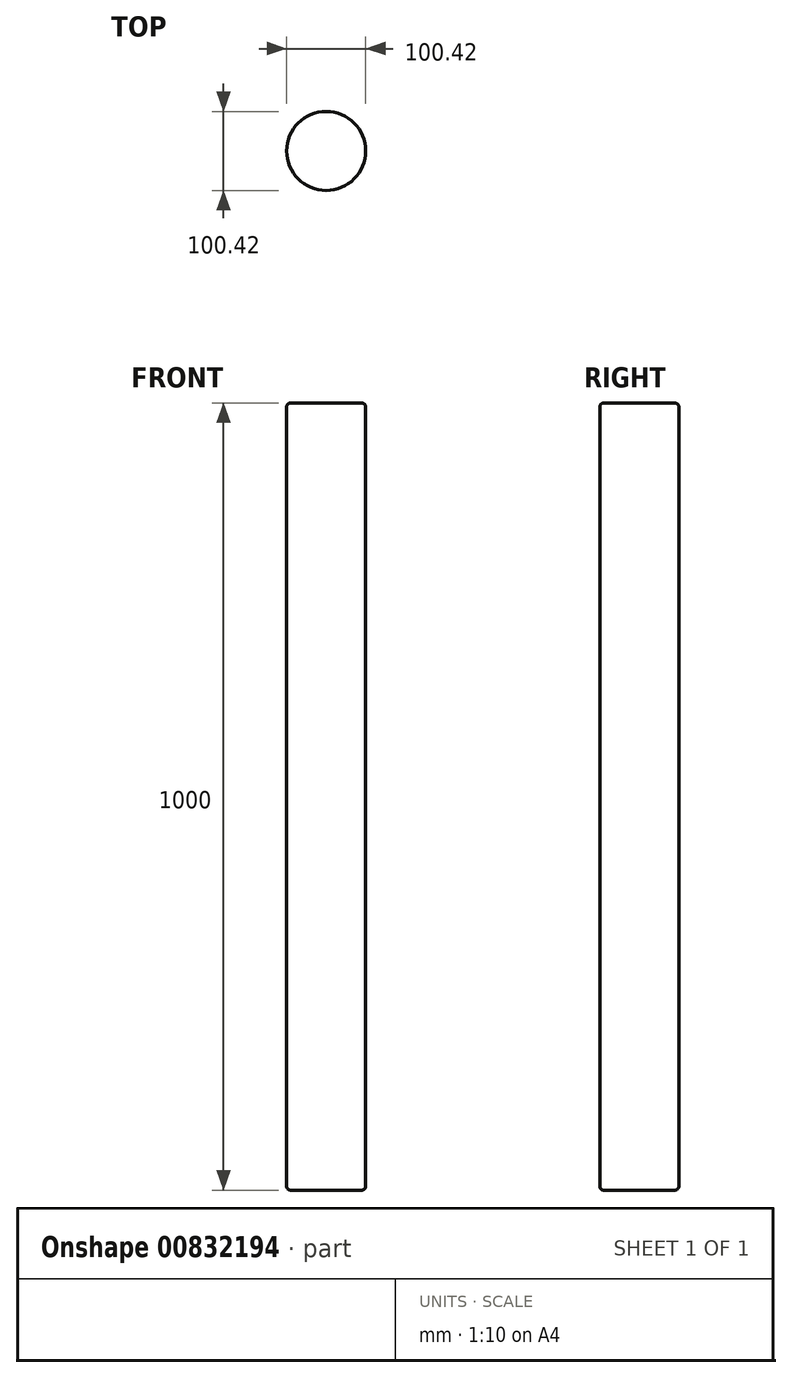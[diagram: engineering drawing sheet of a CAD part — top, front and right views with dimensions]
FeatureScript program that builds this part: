
annotation { "Feature Type Name" : "Feature", "Feature Type Description" : "" }
export const myFeature = defineFeature(function(context is Context, id is Id, definition is map)
    precondition{}
    {
        {
            var Q0;
            Q0=qCreatedBy(makeId("Top.planeOp"),FACE);
            var sketch = newSketch(context, id + "F0", { "sketchPlane" : qUnion([Q0])});
            skCircle(sketch, "E0", {"center": v(0, 0) * mm, "radius": 50.21 * mm});
            skSolve(sketch);
        }
        {
            var Q0;
            Q0 = qSketchRegion(id + "F0", true);
            extrude(context, id + "F1", {"entities" : qUnion([Q0]), "endBound" : BoundingType.SYMMETRIC, "oppositeDirection" : true, "depth" : 1000 * mm, "offsetDistance" : 25.4 * mm});
        }
        {
            var Q0;
            Q0=makeQuery(id+"F1.opExtrude","CAP_EDGE",EDGE,{"disambiguationData":[OSD([sQuery(id+"F0.wireOp",EDGE,"E0")])],"isStart":true});
            fillet(context, id + "F2", {"entities" : qUnion([Q0]), "radius" : 5.08 * mm, "tangentPropagation" : true, "allowEdgeOverflow" : false});
        }
        {
            var Q0;
            Q0=makeQuery(id+"F1.opExtrude","CAP_EDGE",EDGE,{"disambiguationData":[OSD([sQuery(id+"F0.wireOp",EDGE,"E0")])],"isStart":false});
            fillet(context, id + "F3", {"entities" : qUnion([Q0]), "radius" : 5.08 * mm, "tangentPropagation" : true, "allowEdgeOverflow" : false});
        }
    });
